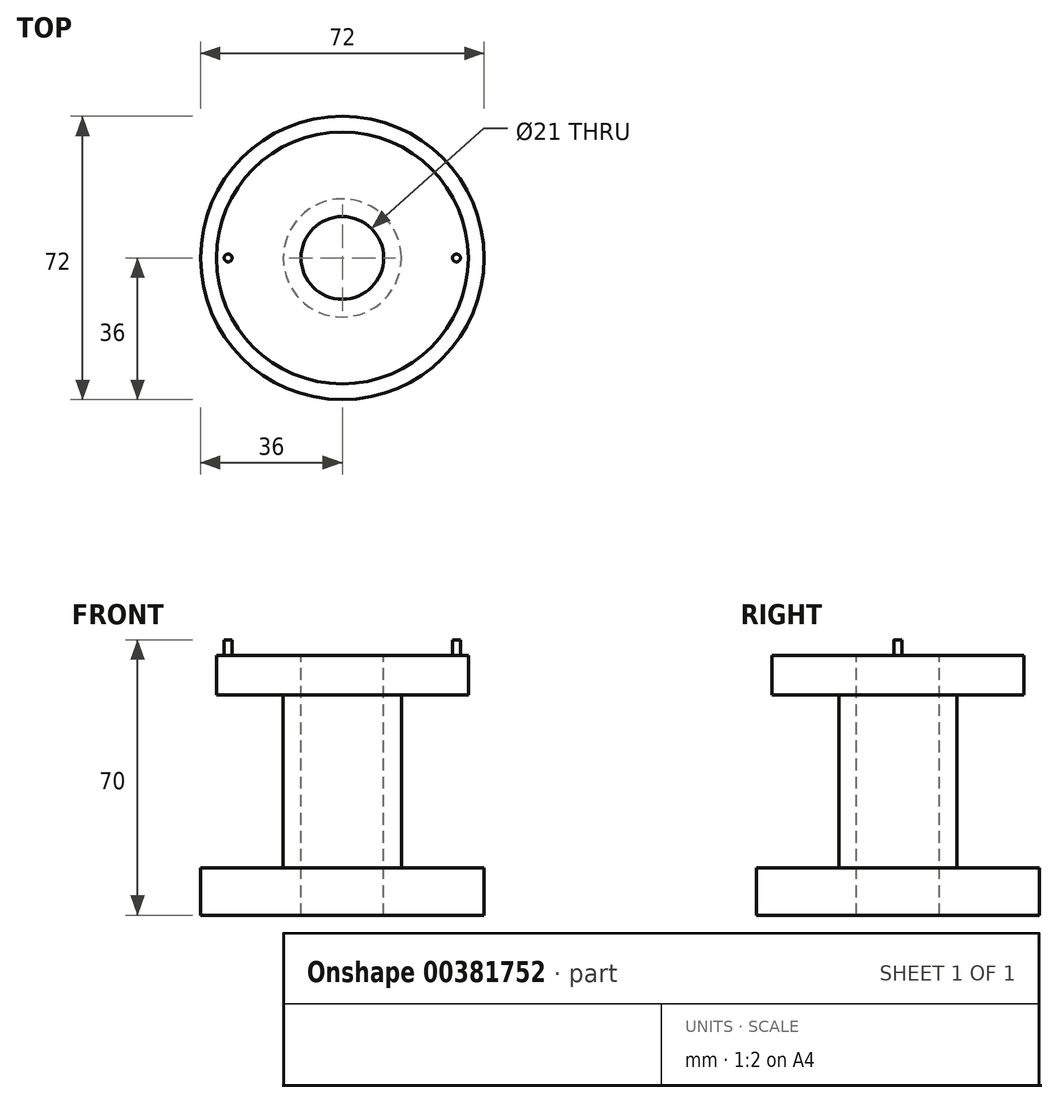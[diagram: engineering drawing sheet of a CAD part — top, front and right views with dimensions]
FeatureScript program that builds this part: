
annotation { "Feature Type Name" : "Feature", "Feature Type Description" : "" }
export const myFeature = defineFeature(function(context is Context, id is Id, definition is map)
    precondition{}
    {
        {
            var Q0;
            Q0=qCreatedBy(makeId("Front.planeOp"),FACE);
            var sketch = newSketch(context, id + "F0", { "sketchPlane" : qUnion([Q0])});
            skLineSegment(sketch, "E0", {"start": v(0, 0) * mm, "end": v(-36, 0) * mm});
            skLineSegment(sketch, "E1", {"start": v(-36, 0) * mm, "end": v(-36, 12) * mm});
            skLineSegment(sketch, "E2", {"start": v(-36, 12) * mm, "end": v(-15, 12) * mm});
            skLineSegment(sketch, "E3", {"start": v(-15, 12) * mm, "end": v(-15, 56) * mm});
            skLineSegment(sketch, "E4", {"start": v(-15, 56) * mm, "end": v(-32, 56) * mm});
            skLineSegment(sketch, "E5", {"start": v(-32, 56) * mm, "end": v(-32, 66) * mm});
            skLineSegment(sketch, "E6", {"start": v(-32, 66) * mm, "end": v(0, 66) * mm});
            skLineSegment(sketch, "E7", {"start": v(0, 66) * mm, "end": v(0, 0) * mm});
            skSolve(sketch);
        }
        {
            var Q0;
            Q0=makeQuery(id+"F0.imprint","IMPRINT",FACE,{"disambiguationData":[TD([[makeQuery(id+"F0.imprint","IMPRINT",EDGE,{"derivedFrom":sQuery(id+"F0.wireOp",EDGE,"E0")}),-1.0]])]});
            var Q1;
            Q1=sQuery(id+"F0.wireOp",EDGE,"E7");
            revolve(context, id + "F1", {"entities" : qUnion([Q0]), "axis" : qUnion([Q1]), "revolveType" : RevolveType.FULL});
        }
        {
            var Q0;
            Q0=makeQuery(id+"F1.opRevolve","SWEPT_FACE",FACE,{"disambiguationData":[OSD([sQuery(id+"F0.wireOp",EDGE,"E6")])]});
            var sketch = newSketch(context, id + "F2", { "sketchPlane" : qUnion([Q0])});
            skCircle(sketch, "E8", {"center": v(0, 0) * mm, "radius": 10.5 * mm});
            skSolve(sketch);
        }
        {
            var Q0;
            Q0=makeQuery(id+"F2.imprint","IMPRINT",FACE,{"disambiguationData":[TD([[makeQuery(id+"F2.imprint","IMPRINT",EDGE,{"derivedFrom":sQuery(id+"F2.wireOp",EDGE,"E8")}),1.0]])]});
            var Q1;
            Q1=sQuery(id+"F2.wireOp",EDGE,"E8");
            extrude(context, id + "F3", {"entities" : qUnion([Q0]), "operationType" : NewBodyOperationType.REMOVE, "surfaceEntities" : qUnion([Q1]), "endBound" : BoundingType.THROUGH_ALL, "oppositeDirection" : true, "depth" : 25 * mm});
        }
        {
            var Q0;
            Q0=makeQuery(id+"F1.opRevolve","SWEPT_FACE",FACE,{"disambiguationData":[OSD([sQuery(id+"F0.wireOp",EDGE,"E6")])]});
            var sketch = newSketch(context, id + "F4", { "sketchPlane" : qUnion([Q0])});
            skCircle(sketch, "E9", {"center": v(-29, 0) * mm, "radius": 1 * mm});
            skCircle(sketch, "E10", {"center": v(29, 0) * mm, "radius": 1 * mm});
            skLineSegment(sketch, "E11", {"start": v(29, 0) * mm, "end": v(-29, 0) * mm, "construction": true});
            skSolve(sketch);
        }
        {
            var Q0;
            Q0 = qSketchRegion(id + "F4", true);
            extrude(context, id + "F5", {"entities" : qUnion([Q0]), "operationType" : NewBodyOperationType.ADD, "depth" : 4 * mm});
        }
    });
